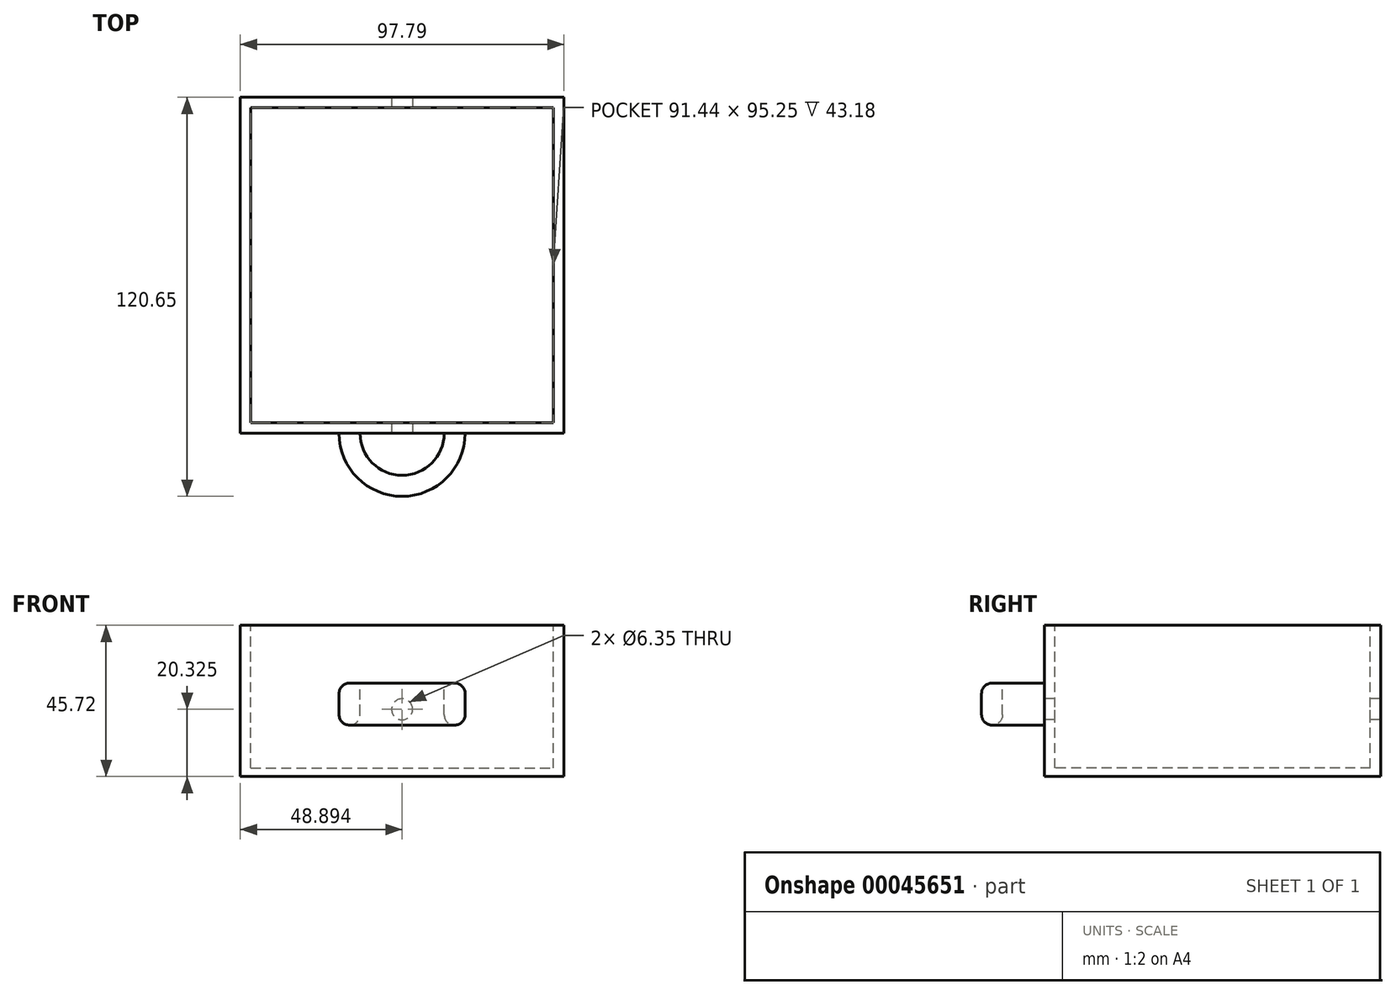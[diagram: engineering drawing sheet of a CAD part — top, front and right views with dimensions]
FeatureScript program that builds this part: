
annotation { "Feature Type Name" : "Feature", "Feature Type Description" : "" }
export const myFeature = defineFeature(function(context is Context, id is Id, definition is map)
    precondition{}
    {
        {
            var Q0;
            Q0=qCreatedBy(makeId("Front.planeOp"),FACE);
            var sketch = newSketch(context, id + "F0", { "sketchPlane" : qUnion([Q0])});
            skLineSegment(sketch, "E0.bottom", {"start": v(-33.41, 27.52) * mm, "end": v(64.38, 27.52) * mm});
            skLineSegment(sketch, "E0.top", {"start": v(-33.41, -18.2) * mm, "end": v(64.38, -18.2) * mm});
            skLineSegment(sketch, "E0.left", {"start": v(-33.41, 27.52) * mm, "end": v(-33.41, -18.2) * mm});
            skLineSegment(sketch, "E0.right", {"start": v(64.38, 27.52) * mm, "end": v(64.38, -18.2) * mm});
            skSolve(sketch);
        }
        {
            var Q0;
            Q0=qSketchRegion(id+"F0",true);
            extrude(context, id + "F1", {"entities" : qUnion([Q0]), "oppositeDirection" : true, "depth" : 101.6 * mm});
        }
        {
            var Q0;
            Q0=makeQuery(id+"F1.opExtrude","SWEPT_FACE",FACE,{"disambiguationData":[OSD([sQuery(id+"F0.wireOp",EDGE,"E0.bottom")])]});
            var sketch = newSketch(context, id + "F2", { "sketchPlane" : qUnion([Q0])});
            skLineSegment(sketch, "E1.bottom", {"start": v(-30.24, 98.43) * mm, "end": v(61.2, 98.43) * mm});
            skLineSegment(sketch, "E1.top", {"start": v(-30.24, 3.17) * mm, "end": v(61.2, 3.18) * mm});
            skLineSegment(sketch, "E1.left", {"start": v(-30.24, 98.43) * mm, "end": v(-30.24, 3.17) * mm});
            skLineSegment(sketch, "E1.right", {"start": v(61.2, 98.43) * mm, "end": v(61.2, 3.18) * mm});
            skSolve(sketch);
        }
        {
            var Q0;
            Q0=qSketchRegion(id+"F2",true);
            extrude(context, id + "F3", {"entities" : qUnion([Q0]), "operationType" : NewBodyOperationType.REMOVE, "oppositeDirection" : true, "depth" : 43.18 * mm});
        }
        {
            var Q0;
            Q0=makeQuery(id+"F1.opExtrude","CAP_FACE",FACE,{"disambiguationData":[OSD([sQuery(id+"F0.wireOp",EDGE,"E0.bottom"),sQuery(id+"F0.wireOp",EDGE,"E0.top"),sQuery(id+"F0.wireOp",EDGE,"E0.left"),sQuery(id+"F0.wireOp",EDGE,"E0.right")])],"isStart":true});
            var sketch = newSketch(context, id + "F4", { "sketchPlane" : qUnion([Q0])});
            skLineSegment(sketch, "E2.bottom", {"start": v(-3.57, 10.06) * mm, "end": v(34.53, 10.06) * mm});
            skLineSegment(sketch, "E2.top", {"start": v(-3.57, -2.64) * mm, "end": v(34.53, -2.64) * mm});
            skLineSegment(sketch, "E2.left", {"start": v(-3.57, 10.06) * mm, "end": v(-3.57, -2.64) * mm});
            skLineSegment(sketch, "E2.right", {"start": v(34.53, 10.06) * mm, "end": v(34.53, -2.64) * mm});
            skLineSegment(sketch, "E3", {"start": v(-3.57, 3.71) * mm, "end": v(34.53, 3.71) * mm});
            skLineSegment(sketch, "E4", {"start": v(15.48, 10.06) * mm, "end": v(15.48, -2.64) * mm});
            skPoint(sketch, "E5", {"position": v(15.48, -18.2) * mm});
            skSolve(sketch);
        }
        {
            var Q0;
            {var subQ3=sQuery(id+"F4.wireOp",EDGE,"E2.bottom");var subQ5=sQuery(id+"F4.wireOp",EDGE,"E2.left");var subQ7=makeQuery(id+"F4.imprint","INTERSECT",VERTEX,{"derivedFrom":[subQ3,subQ5]});Q0=makeQuery(id+"F4.imprint","IMPRINT",FACE,{"disambiguationData":[TD([[makeQuery(id+"F4.imprint","IMPRINT",EDGE,{"disambiguationData":[TD([[subQ7,-1.0]])],"derivedFrom":subQ3}),-1.0]])]});}
            var Q1;
            {var subQ3=sQuery(id+"F4.wireOp",EDGE,"E2.top");var subQ5=sQuery(id+"F4.wireOp",EDGE,"E2.left");var subQ7=makeQuery(id+"F4.imprint","INTERSECT",VERTEX,{"derivedFrom":[subQ3,subQ5]});Q1=makeQuery(id+"F4.imprint","IMPRINT",FACE,{"disambiguationData":[TD([[makeQuery(id+"F4.imprint","IMPRINT",EDGE,{"disambiguationData":[TD([[subQ7,-1.0]])],"derivedFrom":subQ3}),1.0]])]});}
            var Q2;
            Q2=sQuery(id+"F4.wireOp",EDGE,"E4");
            revolve(context, id + "F5", {"operationType" : NewBodyOperationType.ADD, "entities" : qUnion([Q0, Q1]), "axis" : qUnion([Q2]), "revolveType" : RevolveType.ONE_DIRECTION, "oppositeDirection" : true, "angle" : 180 * degree});
        }
        {
            var Q0;
            Q0=makeQuery(id+"F5.opRevolve","SWEPT_FACE",FACE,{"disambiguationData":[OSD([sQuery(id+"F4.wireOp",EDGE,"E2.bottom")])]});
            var sketch = newSketch(context, id + "F6", { "sketchPlane" : qUnion([Q0])});
            skLineSegment(sketch, "E6", {"start": v(2.78, 0) * mm, "end": v(28.18, 0) * mm});
            skArc(sketch, "E7", {"start": v(2.78, 0) * mm, "mid": v(15.48, -12.7) * mm, "end": v(28.18, 0) * mm});
            skSolve(sketch);
        }
        {
            var Q0;
            Q0=qSketchRegion(id+"F6",true);
            extrude(context, id + "F7", {"entities" : qUnion([Q0]), "operationType" : NewBodyOperationType.REMOVE, "oppositeDirection" : true, "depth" : 25.4 * mm});
        }
        {
            var Q0;
            Q0=makeQuery(id+"F5.opRevolve","SWEPT_EDGE",EDGE,{"disambiguationData":[OSD([sQuery(id+"F4.wireOp",EDGE,"E2.bottom"),sQuery(id+"F4.wireOp",EDGE,"E2.left")])]});
            var Q1;
            Q1=makeQuery(id+"F7.boolean.opBoolean","COPY",EDGE,{"derivedFrom":makeQuery(id+"F7.opExtrude","CAP_EDGE",EDGE,{"disambiguationData":[OSD([sQuery(id+"F6.wireOp",EDGE,"E7")])],"isStart":true})});
            var Q2;
            Q2=makeQuery(id+"F5.opRevolve","SWEPT_EDGE",EDGE,{"disambiguationData":[OSD([sQuery(id+"F4.wireOp",EDGE,"E2.top"),sQuery(id+"F4.wireOp",EDGE,"E2.left")])]});
            var Q3;
            Q3=makeQuery(id+"F7.boolean.opBoolean","INTERSECT",EDGE,{"derivedFrom":[makeQuery(id+"F5.opRevolve","SWEPT_FACE",FACE,{"disambiguationData":[OSD([sQuery(id+"F4.wireOp",EDGE,"E2.top")])]}),makeQuery(id+"F7.opExtrude","SWEPT_FACE",FACE,{"disambiguationData":[OSD([sQuery(id+"F6.wireOp",EDGE,"E7")])]})]});
            fillet(context, id + "F8", {"entities" : qUnion([Q0, Q1, Q2, Q3]), "radius" : 3.17 * mm, "tangentPropagation" : true, "allowEdgeOverflow" : false});
        }
        {
            var Q0;
            Q0=makeQuery(id+"F7.boolean.opBoolean","MERGE",FACE,{"derivedFrom":[makeQuery(id+"F1.opExtrude","CAP_FACE",FACE,{"disambiguationData":[OSD([sQuery(id+"F0.wireOp",EDGE,"E0.bottom"),sQuery(id+"F0.wireOp",EDGE,"E0.top"),sQuery(id+"F0.wireOp",EDGE,"E0.left"),sQuery(id+"F0.wireOp",EDGE,"E0.right")])],"isStart":true}),makeQuery(id+"F7.opExtrude","SWEPT_FACE",FACE,{"disambiguationData":[OSD([sQuery(id+"F6.wireOp",EDGE,"E6")])]})]});
            var sketch = newSketch(context, id + "F9", { "sketchPlane" : qUnion([Q0])});
            skPoint(sketch, "E8", {"position": v(15.48, 2.12) * mm});
            skPoint(sketch, "E8.positionSnap0", {"position": v(15.48, 27.52) * mm});
            skSolve(sketch);
        }
        {
            var Q0;
            Q0=sQuery(id+"F9.wireOp",VERTEX,"E8");
            var Q1;
            Q1=makeQuery(id+"F1.opExtrude","SWEPT_BODY",BODY,{"disambiguationData":[OSD([sQuery(id+"F0.wireOp",EDGE,"E0.bottom"),sQuery(id+"F0.wireOp",EDGE,"E0.top"),sQuery(id+"F0.wireOp",EDGE,"E0.left"),sQuery(id+"F0.wireOp",EDGE,"E0.right")])]});
            hole(context, id + "F10", {"style" : HoleStyle.SIMPLE, "holeDiameter" : 6.35 * mm, "endStyle" : HoleEndStyle.THROUGH, "locations" : qUnion([Q0]), "scope" : qUnion([Q1])});
        }
    });
